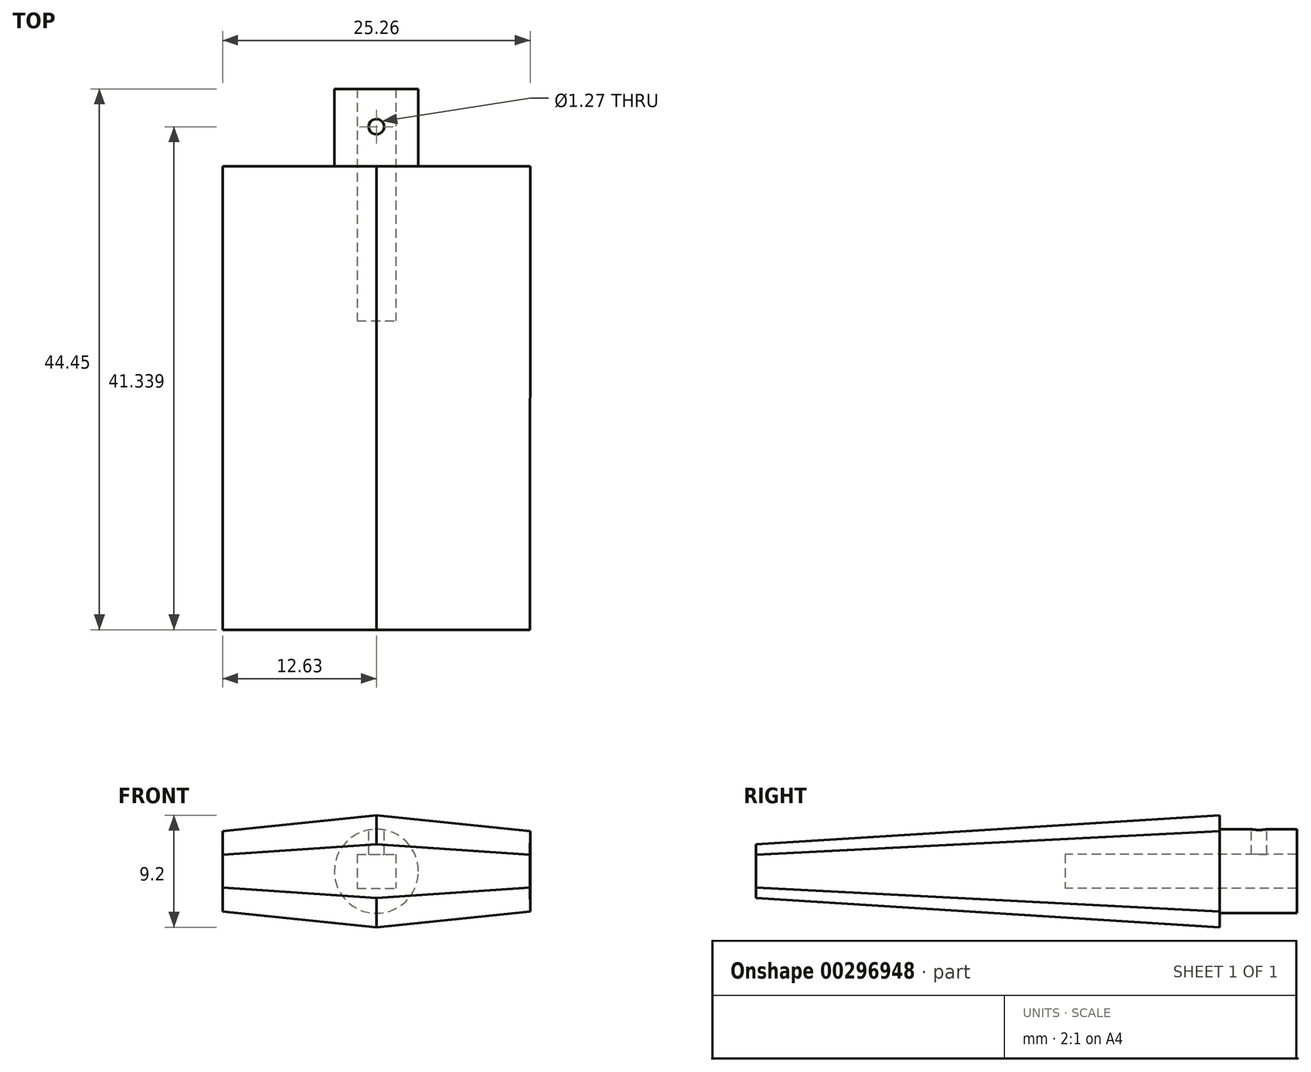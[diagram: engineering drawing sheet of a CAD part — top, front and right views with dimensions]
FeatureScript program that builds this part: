
annotation { "Feature Type Name" : "Feature", "Feature Type Description" : "" }
export const myFeature = defineFeature(function(context is Context, id is Id, definition is map)
    precondition{}
    {
        {
            var Q0;
            Q0=qCreatedBy(makeId("Front.planeOp"),FACE);
            cPlane(context, id + "F0", {"entities" : qUnion([Q0]), "cplaneType" : CPlaneType.OFFSET, "offset" : 38.1 * mm, "width" : 152.4 * mm, "height" : 152.4 * mm});
        }
        {
            var Q0;
            Q0=qCreatedBy(makeId("Front.planeOp"),FACE);
            var sketch = newSketch(context, id + "F1", { "sketchPlane" : qUnion([Q0])});
            skLineSegment(sketch, "E0", {"start": v(0, 4.6) * mm, "end": v(12.63, 3.3) * mm});
            skLineSegment(sketch, "E1", {"start": v(12.63, 3.3) * mm, "end": v(12.63, 0) * mm});
            skLineSegment(sketch, "E2.MirrorCS", {"start": v(12.63, -3.3) * mm, "end": v(12.63, 0) * mm});
            skLineSegment(sketch, "E3.MirrorCS", {"start": v(0, -4.6) * mm, "end": v(12.63, -3.3) * mm});
            skLineSegment(sketch, "E4.MirrorCS", {"start": v(-12.63, -3.3) * mm, "end": v(-12.63, 0) * mm});
            skLineSegment(sketch, "E5.MirrorCS", {"start": v(-12.63, 3.3) * mm, "end": v(-12.63, 0) * mm});
            skLineSegment(sketch, "E6.MirrorCS", {"start": v(0, -4.6) * mm, "end": v(-12.63, -3.3) * mm});
            skLineSegment(sketch, "E7.MirrorCS", {"start": v(0, 4.6) * mm, "end": v(-12.63, 3.3) * mm});
            skSolve(sketch);
        }
        {
            var Q0;
            Q0=qCreatedBy(id+"F0.planeOp",FACE);
            var sketch = newSketch(context, id + "F2", { "sketchPlane" : qUnion([Q0])});
            skLineSegment(sketch, "E8", {"start": v(12.62, 0) * mm, "end": v(12.62, 1.35) * mm});
            skLineSegment(sketch, "E9", {"start": v(12.62, 1.35) * mm, "end": v(0, 2.2) * mm});
            skLineSegment(sketch, "E10.MirrorCS", {"start": v(-12.62, 1.35) * mm, "end": v(0, 2.2) * mm});
            skLineSegment(sketch, "E11.MirrorCS", {"start": v(-12.62, 0) * mm, "end": v(-12.62, 1.35) * mm});
            skLineSegment(sketch, "E12.MirrorCS", {"start": v(12.62, -1.35) * mm, "end": v(0, -2.2) * mm});
            skLineSegment(sketch, "E13.MirrorCS", {"start": v(-12.62, -1.35) * mm, "end": v(0, -2.2) * mm});
            skLineSegment(sketch, "E14.MirrorCS", {"start": v(-12.62, 0) * mm, "end": v(-12.62, -1.35) * mm});
            skLineSegment(sketch, "E15.MirrorCS", {"start": v(12.62, 0) * mm, "end": v(12.62, -1.35) * mm});
            skSolve(sketch);
        }
        {
            var Q0;
            Q0=makeQuery(id+"F1.imprint","IMPRINT",FACE,{"disambiguationData":[TD([[makeQuery(id+"F1.imprint","IMPRINT",EDGE,{"derivedFrom":sQuery(id+"F1.wireOp",EDGE,"E1")}),-1.0]])]});
            var Q1;
            Q1=makeQuery(id+"F2.imprint","IMPRINT",FACE,{"disambiguationData":[TD([[makeQuery(id+"F2.imprint","IMPRINT",EDGE,{"derivedFrom":sQuery(id+"F2.wireOp",EDGE,"E8")}),1.0]])]});
            loft(context, id + "F3", {"sheetProfilesArray" : [{ "sheetProfileEntities" : qUnion([Q0]) }, { "sheetProfileEntities" : qUnion([Q1]) }]});
        }
        {
            var Q0;
            Q0=qCreatedBy(makeId("Front.planeOp"),FACE);
            var sketch = newSketch(context, id + "F4", { "sketchPlane" : qUnion([Q0])});
            skCircle(sketch, "E16", {"center": v(0, 0) * mm, "radius": 3.45 * mm});
            skSolve(sketch);
        }
        {
            var Q0;
            Q0=makeQuery(id+"F4.imprint","IMPRINT",FACE,{"disambiguationData":[TD([[makeQuery(id+"F4.imprint","IMPRINT",EDGE,{"derivedFrom":sQuery(id+"F4.wireOp",EDGE,"E16")}),1.0]])]});
            extrude(context, id + "F5", {"entities" : qUnion([Q0]), "operationType" : NewBodyOperationType.ADD, "oppositeDirection" : true, "depth" : 6.35 * mm});
        }
        {
            var Q0;
            Q0=qCreatedBy(makeId("Front.planeOp"),FACE);
            var sketch = newSketch(context, id + "F6", { "sketchPlane" : qUnion([Q0])});
            skLineSegment(sketch, "E17.bottom", {"start": v(-1.59, 1.4) * mm, "end": v(1.59, 1.4) * mm});
            skLineSegment(sketch, "E17.top", {"start": v(-1.59, -1.4) * mm, "end": v(1.59, -1.4) * mm});
            skLineSegment(sketch, "E17.left", {"start": v(-1.59, 1.4) * mm, "end": v(-1.59, -1.4) * mm});
            skLineSegment(sketch, "E17.right", {"start": v(1.59, 1.4) * mm, "end": v(1.59, -1.4) * mm});
            skPoint(sketch, "E17.middle", {"position": v(0, 0) * mm});
            skSolve(sketch);
        }
        {
            var Q0;
            Q0 = qSketchRegion(id + "F6", true);
            extrude(context, id + "F7", {"entities" : qUnion([Q0]), "operationType" : NewBodyOperationType.REMOVE, "oppositeDirection" : true, "depth" : 25.4 * mm, "offsetDistance" : 25.4 * mm, "hasSecondDirection" : true, "secondDirectionOppositeDirection" : false, "secondDirectionDepth" : 12.7 * mm});
        }
        {
            var Q0;
            Q0=qCreatedBy(makeId("Top.planeOp"),FACE);
            cPlane(context, id + "F8", {"entities" : qUnion([Q0]), "cplaneType" : CPlaneType.OFFSET, "offset" : 6.35 * mm, "width" : 152.4 * mm, "height" : 152.4 * mm});
        }
        {
            var Q0;
            Q0=qCreatedBy(id+"F8.planeOp",FACE);
            var sketch = newSketch(context, id + "F9", { "sketchPlane" : qUnion([Q0])});
            skCircle(sketch, "E18", {"center": v(0, 3.24) * mm, "radius": 0.64 * mm});
            skSolve(sketch);
        }
        {
            var Q0;
            Q0=makeQuery(id+"F9.imprint","IMPRINT",FACE,{"disambiguationData":[TD([[makeQuery(id+"F9.imprint","IMPRINT",EDGE,{"derivedFrom":sQuery(id+"F9.wireOp",EDGE,"E18")}),1.0]])]});
            extrude(context, id + "F10", {"entities" : qUnion([Q0]), "operationType" : NewBodyOperationType.REMOVE, "oppositeDirection" : true, "depth" : 6.35 * mm, "offsetDistance" : 25.4 * mm});
        }
    });
